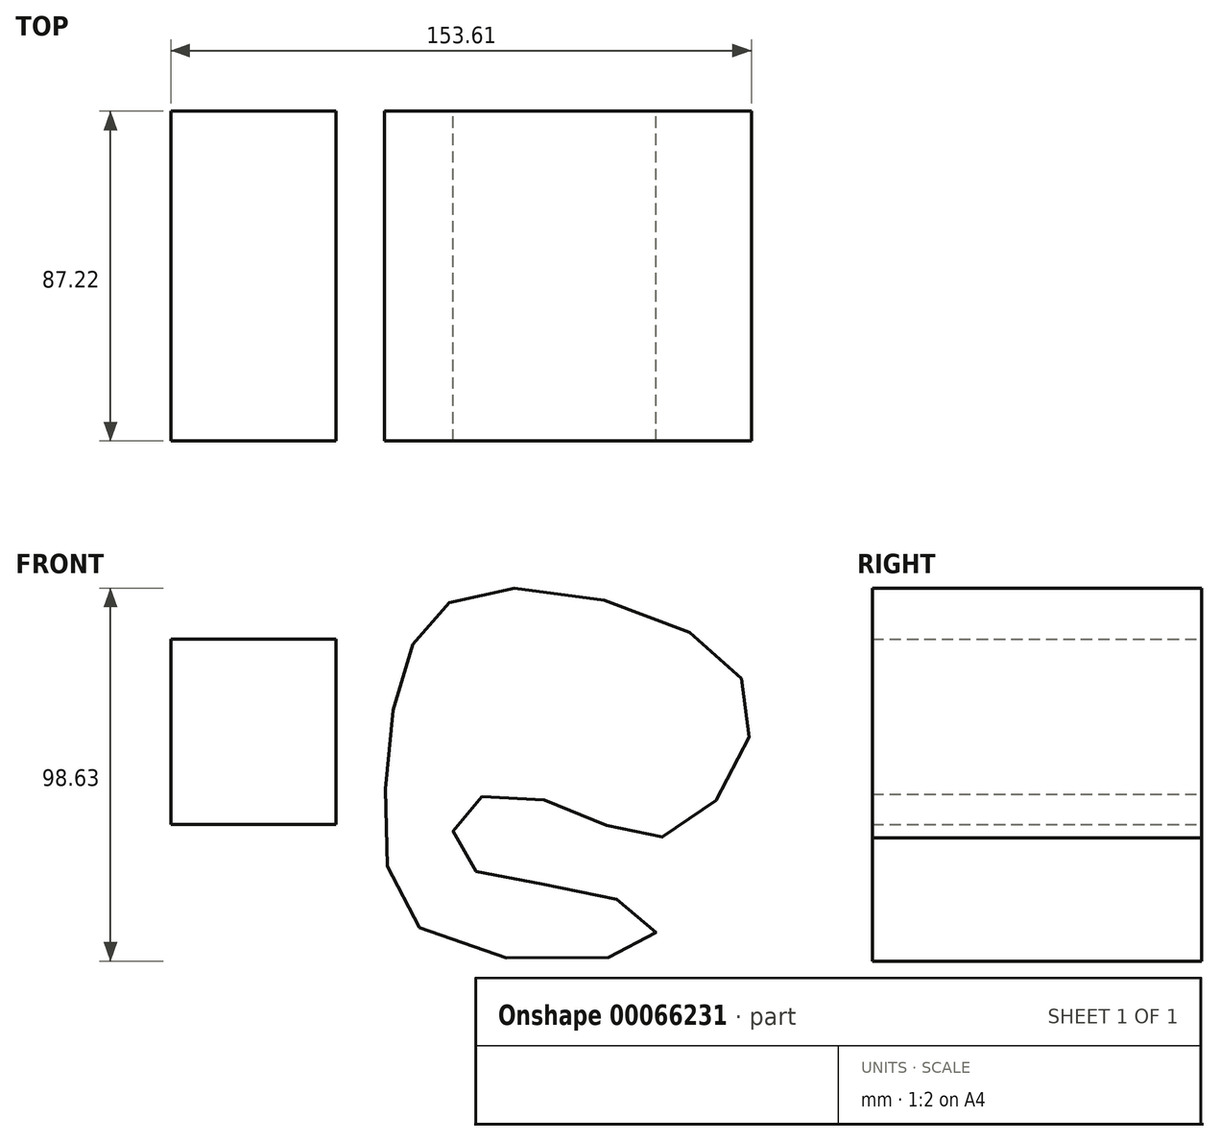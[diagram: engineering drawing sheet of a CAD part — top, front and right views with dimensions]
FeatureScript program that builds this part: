
annotation { "Feature Type Name" : "Feature", "Feature Type Description" : "" }
export const myFeature = defineFeature(function(context is Context, id is Id, definition is map)
    precondition{}
    {
        {
            var Q0;
            Q0=qCreatedBy(makeId("Front.planeOp"),FACE);
            var sketch = newSketch(context, id + "F0", { "sketchPlane" : qUnion([Q0])});
            skLineSegment(sketch, "E0.bottom", {"start": v(-121.95, 59.6) * mm, "end": v(-78.3, 59.6) * mm});
            skLineSegment(sketch, "E0.top", {"start": v(-121.95, 10.55) * mm, "end": v(-78.3, 10.55) * mm});
            skLineSegment(sketch, "E0.left", {"start": v(-121.95, 59.6) * mm, "end": v(-121.95, 10.55) * mm});
            skLineSegment(sketch, "E0.right", {"start": v(-78.3, 59.6) * mm, "end": v(-78.3, 10.55) * mm});
            skFitSpline(sketch, "E1", {"points": [v(-57.97, 58.15) * mm, v(-65.4, 15.93) * mm, v(-51.74, -19.6) * mm, v(5.85, -19.9) * mm, v(-8.4, -7.7) * mm, v(-44.02, 0) * mm, v(-44.61, 15.1) * mm, v(-18.5, 15.52) * mm, v(8.82, 7.37) * mm, v(31.08, 33.98) * mm, v(19.5, 58.84) * mm, v(-37.79, 72.58) * mm, v(-57.97, 58.15) * mm]});
            skSolve(sketch);
        }
        {
            var Q0;
            Q0=makeQuery(id+"F0.imprint","IMPRINT",FACE,{"disambiguationData":[TD([[makeQuery(id+"F0.imprint","IMPRINT",EDGE,{"derivedFrom":sQuery(id+"F0.wireOp",EDGE,"E1")}),1.0]])]});
            var Q1;
            Q1=makeQuery(id+"F0.imprint","IMPRINT",FACE,{"disambiguationData":[TD([[makeQuery(id+"F0.imprint","IMPRINT",EDGE,{"derivedFrom":sQuery(id+"F0.wireOp",EDGE,"E0.bottom")}),-1.0]])]});
            extrude(context, id + "F1", {"entities" : qUnion([Q0, Q1]), "depth" : 87.22 * mm});
        }
    });
